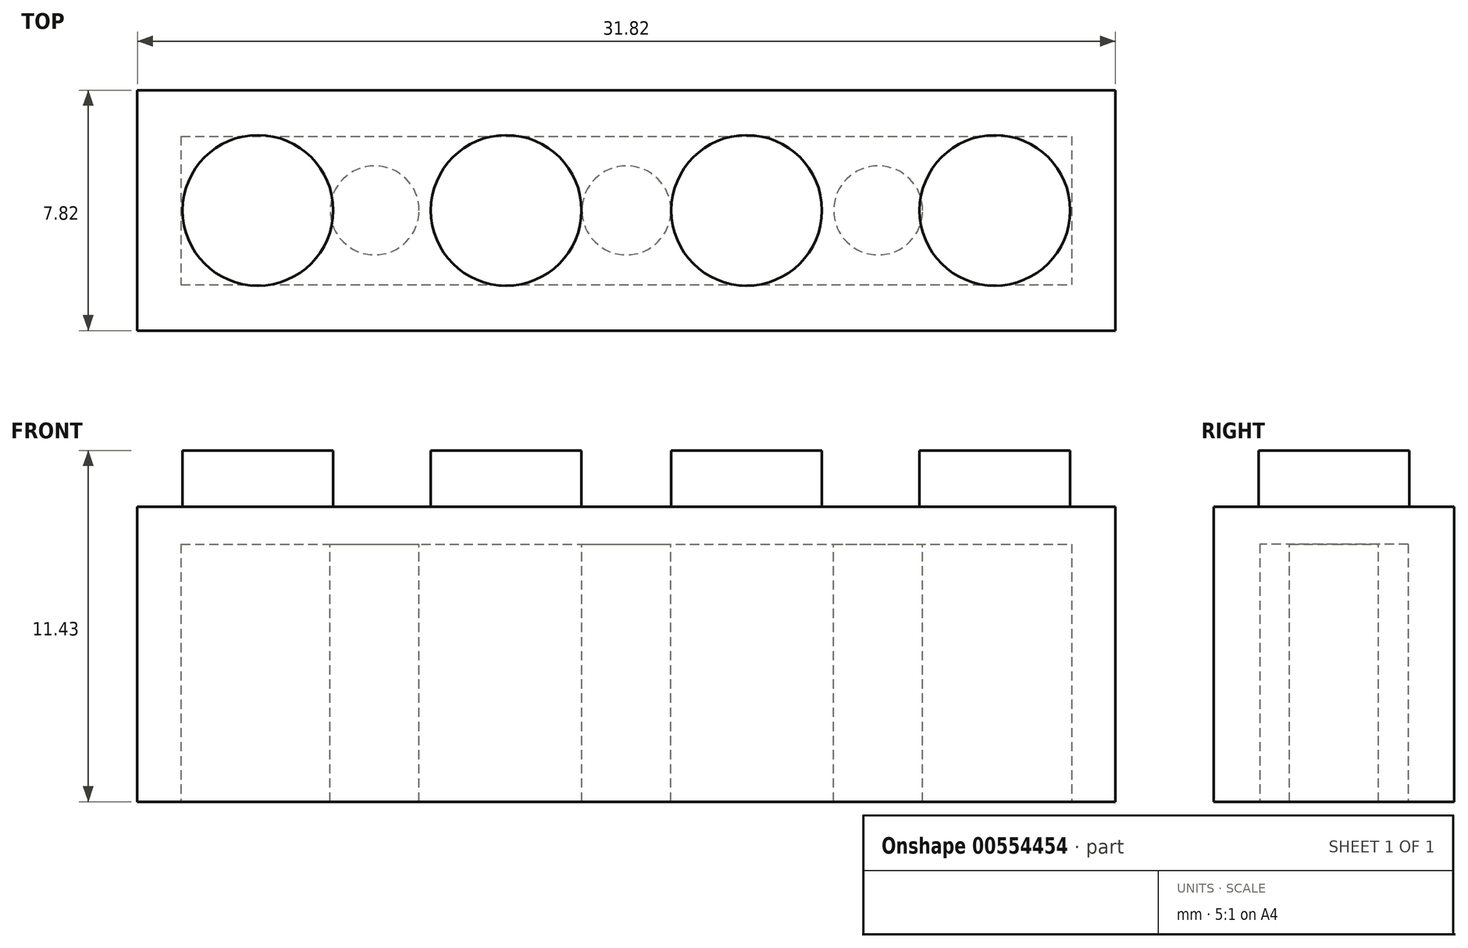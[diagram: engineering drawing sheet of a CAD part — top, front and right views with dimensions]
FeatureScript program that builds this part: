
annotation { "Feature Type Name" : "Feature", "Feature Type Description" : "" }
export const myFeature = defineFeature(function(context is Context, id is Id, definition is map)
    precondition{}
    {
        {
            var Q0;
            Q0=qCreatedBy(makeId("Top.planeOp"),FACE);
            var sketch = newSketch(context, id + "F0", { "sketchPlane" : qUnion([Q0])});
            skLineSegment(sketch, "E0.bottom", {"start": v(-15.91, 3.91) * mm, "end": v(15.91, 3.91) * mm});
            skLineSegment(sketch, "E0.top", {"start": v(-15.91, -3.91) * mm, "end": v(15.91, -3.91) * mm});
            skLineSegment(sketch, "E0.left", {"start": v(-15.91, 3.91) * mm, "end": v(-15.91, -3.91) * mm});
            skLineSegment(sketch, "E0.right", {"start": v(15.91, 3.91) * mm, "end": v(15.91, -3.91) * mm});
            skPoint(sketch, "E0.middle", {"position": v(0, 0) * mm});
            skSolve(sketch);
        }
        {
            var Q0;
            Q0 = qSketchRegion(id + "F0", true);
            extrude(context, id + "F1", {"entities" : qUnion([Q0]), "depth" : 9.6 * mm, "offsetDistance" : 25.4 * mm});
        }
        {
            var Q0;
            Q0=makeQuery(id+"F1.opExtrude","CAP_FACE",FACE,{"disambiguationData":[OSD([sQuery(id+"F0.wireOp",EDGE,"E0.bottom"),sQuery(id+"F0.wireOp",EDGE,"E0.top"),sQuery(id+"F0.wireOp",EDGE,"E0.left"),sQuery(id+"F0.wireOp",EDGE,"E0.right")])],"isStart":false});
            var sketch = newSketch(context, id + "F2", { "sketchPlane" : qUnion([Q0])});
            skSolve(sketch);
        }
        {
            var Q0;
            Q0=makeQuery(id+"F2.imprint","IMPRINT",FACE,{"disambiguationData":[TD([[makeQuery(id+"F2.imprint","IMPRINT",EDGE,{"derivedFrom":makeQuery(id+"F1.opExtrude","CAP_EDGE",EDGE,{"disambiguationData":[OSD([sQuery(id+"F0.wireOp",EDGE,"E0.bottom")])],"isStart":false})}),-1.0]])]});
            var sketch = newSketch(context, id + "F3", { "sketchPlane" : qUnion([Q0])});
            skCircle(sketch, "E1", {"center": v(-11.99, 0) * mm, "radius": 2.45 * mm});
            skCircle(sketch, "E2", {"center": v(-3.91, 0) * mm, "radius": 2.45 * mm});
            skCircle(sketch, "E3", {"center": v(3.91, 0) * mm, "radius": 2.45 * mm});
            skCircle(sketch, "E4", {"center": v(11.99, 0) * mm, "radius": 2.45 * mm});
            skSolve(sketch);
        }
        {
            var Q0;
            Q0=makeQuery(id+"F3.imprint","IMPRINT",FACE,{"disambiguationData":[TD([[makeQuery(id+"F3.imprint","IMPRINT",EDGE,{"derivedFrom":sQuery(id+"F3.wireOp",EDGE,"E4")}),1.0]])]});
            var Q1;
            Q1=makeQuery(id+"F3.imprint","IMPRINT",FACE,{"disambiguationData":[TD([[makeQuery(id+"F3.imprint","IMPRINT",EDGE,{"derivedFrom":sQuery(id+"F3.wireOp",EDGE,"E3")}),1.0]])]});
            var Q2;
            Q2=makeQuery(id+"F3.imprint","IMPRINT",FACE,{"disambiguationData":[TD([[makeQuery(id+"F3.imprint","IMPRINT",EDGE,{"derivedFrom":sQuery(id+"F3.wireOp",EDGE,"E2")}),1.0]])]});
            var Q3;
            Q3=makeQuery(id+"F3.imprint","IMPRINT",FACE,{"disambiguationData":[TD([[makeQuery(id+"F3.imprint","IMPRINT",EDGE,{"derivedFrom":sQuery(id+"F3.wireOp",EDGE,"E1")}),1.0]])]});
            extrude(context, id + "F4", {"entities" : qUnion([Q0, Q1, Q2, Q3]), "operationType" : NewBodyOperationType.ADD, "depth" : 1.83 * mm, "offsetDistance" : 25.4 * mm});
        }
        {
            var Q0;
            Q0=makeQuery(id+"F1.opExtrude","CAP_FACE",FACE,{"disambiguationData":[OSD([sQuery(id+"F0.wireOp",EDGE,"E0.bottom"),sQuery(id+"F0.wireOp",EDGE,"E0.top"),sQuery(id+"F0.wireOp",EDGE,"E0.left"),sQuery(id+"F0.wireOp",EDGE,"E0.right")])],"isStart":true});
            var sketch = newSketch(context, id + "F5", { "sketchPlane" : qUnion([Q0])});
            skLineSegment(sketch, "E5.bottom", {"start": v(-14.5, -2.41) * mm, "end": v(14.5, -2.41) * mm});
            skLineSegment(sketch, "E5.top", {"start": v(-14.5, 2.41) * mm, "end": v(14.5, 2.41) * mm});
            skLineSegment(sketch, "E5.left", {"start": v(-14.5, -2.41) * mm, "end": v(-14.5, 2.41) * mm});
            skLineSegment(sketch, "E5.right", {"start": v(14.5, -2.41) * mm, "end": v(14.5, 2.41) * mm});
            skPoint(sketch, "E5.middle", {"position": v(0, 0) * mm});
            skSolve(sketch);
        }
        {
            var Q0;
            Q0=makeQuery(id+"F5.imprint","IMPRINT",FACE,{"disambiguationData":[TD([[makeQuery(id+"F5.imprint","IMPRINT",EDGE,{"derivedFrom":sQuery(id+"F5.wireOp",EDGE,"E5.bottom")}),1.0]])]});
            extrude(context, id + "F6", {"entities" : qUnion([Q0]), "operationType" : NewBodyOperationType.REMOVE, "oppositeDirection" : true, "depth" : 8.38 * mm, "offsetDistance" : 25.4 * mm});
        }
        {
            var Q0;
            Q0=makeQuery(id+"F6.boolean.opBoolean","COPY",FACE,{"derivedFrom":makeQuery(id+"F6.opExtrude","CAP_FACE",FACE,{"disambiguationData":[OSD([sQuery(id+"F5.wireOp",EDGE,"E5.bottom"),sQuery(id+"F5.wireOp",EDGE,"E5.top"),sQuery(id+"F5.wireOp",EDGE,"E5.left"),sQuery(id+"F5.wireOp",EDGE,"E5.right")])],"isStart":false})});
            var sketch = newSketch(context, id + "F7", { "sketchPlane" : qUnion([Q0])});
            skCircle(sketch, "E6", {"center": v(0, 0) * mm, "radius": 1.45 * mm});
            skCircle(sketch, "E7", {"center": v(-8.2, 0) * mm, "radius": 1.45 * mm});
            skCircle(sketch, "E8", {"center": v(8.2, 0) * mm, "radius": 1.45 * mm});
            skSolve(sketch);
        }
        {
            var Q0;
            Q0=makeQuery(id+"F7.imprint","IMPRINT",FACE,{"disambiguationData":[TD([[makeQuery(id+"F7.imprint","IMPRINT",EDGE,{"derivedFrom":sQuery(id+"F7.wireOp",EDGE,"E7")}),1.0]])]});
            var Q1;
            Q1=makeQuery(id+"F7.imprint","IMPRINT",FACE,{"disambiguationData":[TD([[makeQuery(id+"F7.imprint","IMPRINT",EDGE,{"derivedFrom":sQuery(id+"F7.wireOp",EDGE,"E6")}),1.0]])]});
            var Q2;
            Q2=makeQuery(id+"F7.imprint","IMPRINT",FACE,{"disambiguationData":[TD([[makeQuery(id+"F7.imprint","IMPRINT",EDGE,{"derivedFrom":sQuery(id+"F7.wireOp",EDGE,"E8")}),1.0]])]});
            extrude(context, id + "F8", {"entities" : qUnion([Q0, Q1, Q2]), "operationType" : NewBodyOperationType.ADD, "depth" : 8.38 * mm, "offsetDistance" : 25.4 * mm});
        }
    });
